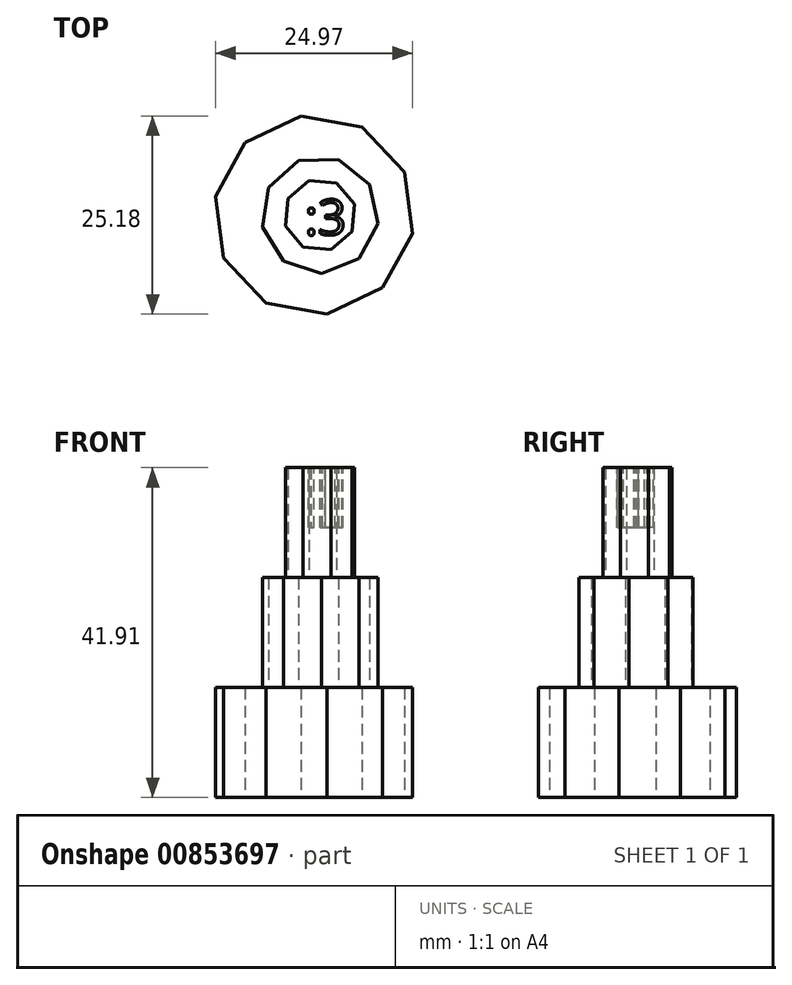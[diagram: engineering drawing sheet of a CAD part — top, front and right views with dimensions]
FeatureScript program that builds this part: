
annotation { "Feature Type Name" : "Feature", "Feature Type Description" : "" }
export const myFeature = defineFeature(function(context is Context, id is Id, definition is map)
    precondition{}
    {
        {
            var Q0;
            Q0=qCreatedBy(makeId("Top.planeOp"),FACE);
            var sketch = newSketch(context, id + "F0", { "sketchPlane" : qUnion([Q0])});
            skCircle(sketch, "E0.cCircle", {"center": v(-0.76, 0) * mm, "radius": 12.08 * mm, "construction": true});
            skLineSegment(sketch, "E0.0", {"start": v(11.73, -2.34) * mm, "end": v(7.97, -9.23) * mm});
            skLineSegment(sketch, "E0.1", {"start": v(7.97, -9.23) * mm, "end": v(0.88, -12.6) * mm});
            skLineSegment(sketch, "E0.2", {"start": v(0.88, -12.6) * mm, "end": v(-6.84, -11.15) * mm});
            skLineSegment(sketch, "E0.3", {"start": v(-6.84, -11.15) * mm, "end": v(-12.23, -5.45) * mm});
            skLineSegment(sketch, "E0.4", {"start": v(-12.23, -5.45) * mm, "end": v(-13.24, 2.34) * mm});
            skLineSegment(sketch, "E0.5", {"start": v(-13.24, 2.34) * mm, "end": v(-9.48, 9.23) * mm});
            skLineSegment(sketch, "E0.6", {"start": v(-9.48, 9.23) * mm, "end": v(-2.4, 12.6) * mm});
            skLineSegment(sketch, "E0.7", {"start": v(-2.4, 12.6) * mm, "end": v(5.32, 11.15) * mm});
            skLineSegment(sketch, "E0.8", {"start": v(5.32, 11.15) * mm, "end": v(10.71, 5.45) * mm});
            skLineSegment(sketch, "E0.9", {"start": v(10.71, 5.45) * mm, "end": v(11.73, -2.34) * mm});
            skPoint(sketch, "E0.0.midPoint", {"position": v(9.85, -5.78) * mm});
            skSolve(sketch);
        }
        {
            var Q0;
            Q0 = qSketchRegion(id + "F0", true);
            extrude(context, id + "F1", {"entities" : qUnion([Q0]), "depth" : 13.97 * mm, "offsetDistance" : 25.4 * mm});
        }
        {
            var Q0;
            Q0=qCreatedBy(makeId("Top.planeOp"),FACE);
            var sketch = newSketch(context, id + "F2", { "sketchPlane" : qUnion([Q0])});
            skCircle(sketch, "E1.cCircle", {"center": v(0, 0) * mm, "radius": 6.98 * mm, "construction": true});
            skLineSegment(sketch, "E1.0", {"start": v(7.35, -1.07) * mm, "end": v(4.94, -5.54) * mm});
            skLineSegment(sketch, "E1.1", {"start": v(4.94, -5.54) * mm, "end": v(0.22, -7.42) * mm});
            skLineSegment(sketch, "E1.2", {"start": v(0.22, -7.42) * mm, "end": v(-4.6, -5.83) * mm});
            skLineSegment(sketch, "E1.3", {"start": v(-4.6, -5.83) * mm, "end": v(-7.27, -1.5) * mm});
            skLineSegment(sketch, "E1.4", {"start": v(-7.27, -1.5) * mm, "end": v(-6.54, 3.52) * mm});
            skLineSegment(sketch, "E1.5", {"start": v(-6.54, 3.52) * mm, "end": v(-2.74, 6.9) * mm});
            skLineSegment(sketch, "E1.6", {"start": v(-2.74, 6.9) * mm, "end": v(2.33, 7.05) * mm});
            skLineSegment(sketch, "E1.7", {"start": v(2.33, 7.05) * mm, "end": v(6.32, 3.9) * mm});
            skLineSegment(sketch, "E1.8", {"start": v(6.32, 3.9) * mm, "end": v(7.35, -1.07) * mm});
            skPoint(sketch, "E1.0.midPoint", {"position": v(6.14, -3.3) * mm});
            skSolve(sketch);
        }
        {
            var Q0;
            Q0 = qSketchRegion(id + "F2", true);
            extrude(context, id + "F3", {"entities" : qUnion([Q0]), "operationType" : NewBodyOperationType.ADD, "depth" : 27.94 * mm, "offsetDistance" : 25.4 * mm});
        }
        {
            var Q0;
            Q0=qCreatedBy(makeId("Top.planeOp"),FACE);
            var sketch = newSketch(context, id + "F4", { "sketchPlane" : qUnion([Q0])});
            skCircle(sketch, "E2.cCircle", {"center": v(0, 0) * mm, "radius": 4.25 * mm, "construction": true});
            skLineSegment(sketch, "E2.0", {"start": v(2.12, 4.09) * mm, "end": v(4.4, 1.39) * mm});
            skLineSegment(sketch, "E2.1", {"start": v(4.4, 1.39) * mm, "end": v(4.09, -2.12) * mm});
            skLineSegment(sketch, "E2.2", {"start": v(4.09, -2.12) * mm, "end": v(1.39, -4.4) * mm});
            skLineSegment(sketch, "E2.3", {"start": v(1.39, -4.4) * mm, "end": v(-2.12, -4.09) * mm});
            skLineSegment(sketch, "E2.4", {"start": v(-2.12, -4.09) * mm, "end": v(-4.4, -1.39) * mm});
            skLineSegment(sketch, "E2.5", {"start": v(-4.4, -1.39) * mm, "end": v(-4.09, 2.12) * mm});
            skLineSegment(sketch, "E2.6", {"start": v(-4.09, 2.12) * mm, "end": v(-1.39, 4.4) * mm});
            skLineSegment(sketch, "E2.7", {"start": v(-1.39, 4.4) * mm, "end": v(2.12, 4.09) * mm});
            skPoint(sketch, "E2.0.midPoint", {"position": v(3.26, 2.74) * mm});
            skSolve(sketch);
        }
        {
            var Q0;
            Q0 = qSketchRegion(id + "F4", true);
            extrude(context, id + "F5", {"entities" : qUnion([Q0]), "operationType" : NewBodyOperationType.ADD, "depth" : 41.9 * mm, "offsetDistance" : 25.4 * mm});
        }
        {
            var Q0;
            Q0=makeQuery(id+"F5.opExtrude","CAP_FACE",FACE,{"disambiguationData":[OSD([sQuery(id+"F4.wireOp",EDGE,"E2.0"),sQuery(id+"F4.wireOp",EDGE,"E2.1"),sQuery(id+"F4.wireOp",EDGE,"E2.2"),sQuery(id+"F4.wireOp",EDGE,"E2.3"),sQuery(id+"F4.wireOp",EDGE,"E2.4"),sQuery(id+"F4.wireOp",EDGE,"E2.5"),sQuery(id+"F4.wireOp",EDGE,"E2.6"),sQuery(id+"F4.wireOp",EDGE,"E2.7")])],"isStart":false});
            var sketch = newSketch(context, id + "F6", { "sketchPlane" : qUnion([Q0])});
            skText(sketch, "E3", { "text": ":3", "fontName": "OpenSans-Regular.ttf"});
            const initialGuessF6  = {"E3": [-0.00193, -0.00251, 1, 0, 0.0045]};
            skSetInitialGuess(sketch, initialGuessF6);
            skSolve(sketch);
        }
        {
            var Q0;
            Q0 = qSketchRegion(id + "F6", true);
            extrude(context, id + "F7", {"entities" : qUnion([Q0]), "operationType" : NewBodyOperationType.REMOVE, "oppositeDirection" : true, "depth" : 7.62 * mm, "offsetDistance" : 25.4 * mm, "hasSecondDirection" : true, "secondDirectionOppositeDirection" : false, "secondDirectionDepth" : 25.4 * mm});
        }
    });
